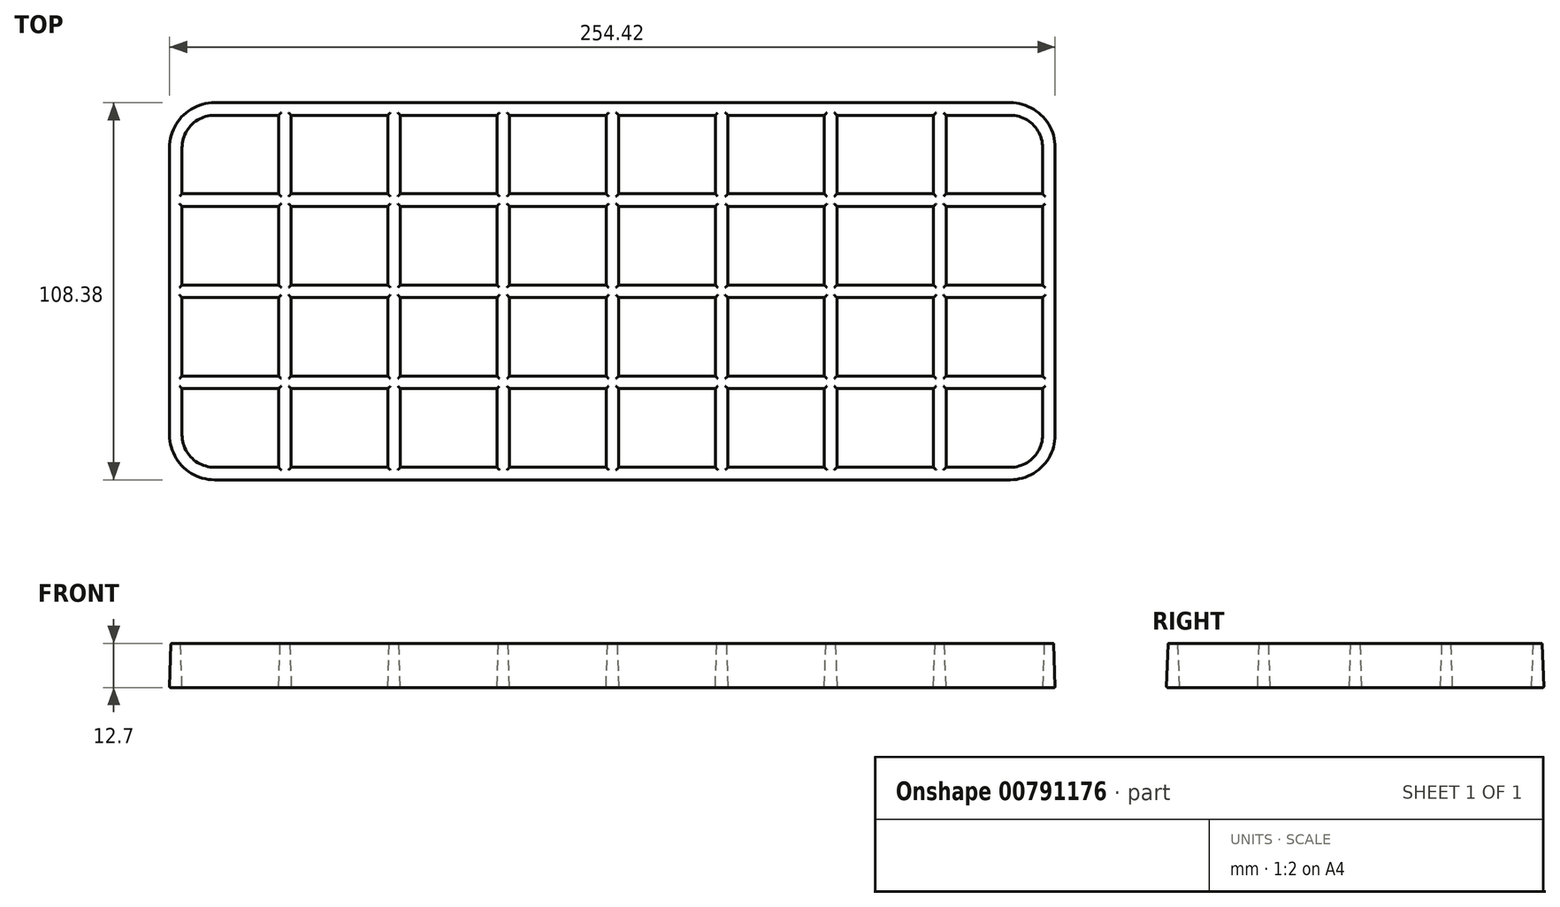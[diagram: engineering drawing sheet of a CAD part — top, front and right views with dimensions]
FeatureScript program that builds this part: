
annotation { "Feature Type Name" : "Feature", "Feature Type Description" : "" }
export const myFeature = defineFeature(function(context is Context, id is Id, definition is map)
    precondition{}
    {
        {
            var Q0;
            Q0=qCreatedBy(makeId("Top.planeOp"),FACE);
            var sketch = newSketch(context, id + "F0", { "sketchPlane" : qUnion([Q0])});
            skLineSegment(sketch, "E0.bottom", {"start": v(114.3, 53.98) * mm, "end": v(-114.3, 53.98) * mm});
            skLineSegment(sketch, "E0.top", {"start": v(114.3, -53.98) * mm, "end": v(-114.3, -53.98) * mm});
            skLineSegment(sketch, "E0.left", {"start": v(127, 41.27) * mm, "end": v(127, -41.27) * mm});
            skLineSegment(sketch, "E0.right", {"start": v(-127, 41.27) * mm, "end": v(-127, -41.27) * mm});
            skPoint(sketch, "E0.middle", {"position": v(0, 0) * mm});
            skLineSegment(sketch, "E1", {"start": v(-123.83, 26.2) * mm, "end": v(123.82, 26.2) * mm, "construction": true});
            skLineSegment(sketch, "E2", {"start": v(-123.82, 0) * mm, "end": v(123.82, 0) * mm, "construction": true});
            skLineSegment(sketch, "E3", {"start": v(-123.82, -26.2) * mm, "end": v(123.82, -26.2) * mm, "construction": true});
            skLineSegment(sketch, "E4", {"start": v(-94.06, 50.8) * mm, "end": v(-94.06, -50.8) * mm, "construction": true});
            skLineSegment(sketch, "E5", {"start": v(-62.7, 50.8) * mm, "end": v(-62.7, -50.8) * mm, "construction": true});
            skLineSegment(sketch, "E6", {"start": v(-31.35, 50.8) * mm, "end": v(-31.35, -50.8) * mm, "construction": true});
            skLineSegment(sketch, "E7", {"start": v(0, 50.8) * mm, "end": v(0, -50.8) * mm, "construction": true});
            skLineSegment(sketch, "E8", {"start": v(31.35, 50.8) * mm, "end": v(31.35, -50.8) * mm, "construction": true});
            skLineSegment(sketch, "E9", {"start": v(62.7, -50.8) * mm, "end": v(62.7, 50.8) * mm, "construction": true});
            skLineSegment(sketch, "E10", {"start": v(94.06, 50.8) * mm, "end": v(94.06, -50.8) * mm, "construction": true});
            skLineSegment(sketch, "E11.bottom", {"start": v(123.82, 27.78) * mm, "end": v(-123.83, 27.78) * mm});
            skLineSegment(sketch, "E11.top", {"start": v(123.82, 24.6) * mm, "end": v(-123.83, 24.6) * mm});
            skLineSegment(sketch, "E11.left", {"start": v(123.82, 27.78) * mm, "end": v(123.82, 24.6) * mm});
            skLineSegment(sketch, "E11.right", {"start": v(-123.82, 27.78) * mm, "end": v(-123.82, 24.6) * mm});
            skPoint(sketch, "E11.middle", {"position": v(0, 26.2) * mm});
            skLineSegment(sketch, "E12.bottom", {"start": v(123.82, 1.59) * mm, "end": v(-123.82, 1.59) * mm});
            skLineSegment(sketch, "E12.top", {"start": v(123.82, -1.59) * mm, "end": v(-123.82, -1.59) * mm});
            skLineSegment(sketch, "E12.left", {"start": v(123.82, 1.59) * mm, "end": v(123.82, -1.59) * mm});
            skLineSegment(sketch, "E12.right", {"start": v(-123.82, 1.59) * mm, "end": v(-123.82, -1.59) * mm});
            skLineSegment(sketch, "E13.bottom", {"start": v(123.82, -24.6) * mm, "end": v(-123.82, -24.6) * mm});
            skLineSegment(sketch, "E13.top", {"start": v(123.82, -27.78) * mm, "end": v(-123.82, -27.78) * mm});
            skLineSegment(sketch, "E13.left", {"start": v(123.82, -24.6) * mm, "end": v(123.82, -27.78) * mm});
            skLineSegment(sketch, "E13.right", {"start": v(-123.82, -24.6) * mm, "end": v(-123.82, -27.78) * mm});
            skPoint(sketch, "E13.middle", {"position": v(0, -26.2) * mm});
            skLineSegment(sketch, "E14.bottom", {"start": v(-92.47, 50.8) * mm, "end": v(-95.65, 50.8) * mm});
            skLineSegment(sketch, "E14.top", {"start": v(-92.47, -50.8) * mm, "end": v(-95.65, -50.8) * mm});
            skLineSegment(sketch, "E14.left", {"start": v(-92.47, 50.8) * mm, "end": v(-92.47, -50.8) * mm});
            skLineSegment(sketch, "E14.right", {"start": v(-95.65, 50.8) * mm, "end": v(-95.65, -50.8) * mm});
            skPoint(sketch, "E14.middle", {"position": v(-94.06, 0) * mm});
            skLineSegment(sketch, "E15.bottom", {"start": v(-61.12, 50.8) * mm, "end": v(-64.3, 50.8) * mm});
            skLineSegment(sketch, "E15.top", {"start": v(-61.12, -50.8) * mm, "end": v(-64.3, -50.8) * mm});
            skLineSegment(sketch, "E15.left", {"start": v(-61.12, 50.8) * mm, "end": v(-61.12, -50.8) * mm});
            skLineSegment(sketch, "E15.right", {"start": v(-64.3, 50.8) * mm, "end": v(-64.3, -50.8) * mm});
            skPoint(sketch, "E15.middle", {"position": v(-62.7, 0) * mm});
            skLineSegment(sketch, "E16.bottom", {"start": v(-29.77, 50.8) * mm, "end": v(-32.94, 50.8) * mm});
            skLineSegment(sketch, "E16.top", {"start": v(-29.77, -50.8) * mm, "end": v(-32.94, -50.8) * mm});
            skLineSegment(sketch, "E16.left", {"start": v(-29.77, 50.8) * mm, "end": v(-29.77, -50.8) * mm});
            skLineSegment(sketch, "E16.right", {"start": v(-32.94, 50.8) * mm, "end": v(-32.94, -50.8) * mm});
            skPoint(sketch, "E16.middle", {"position": v(-31.35, 0) * mm});
            skLineSegment(sketch, "E17.bottom", {"start": v(1.59, 50.8) * mm, "end": v(-1.59, 50.8) * mm});
            skLineSegment(sketch, "E17.top", {"start": v(1.59, -50.8) * mm, "end": v(-1.59, -50.8) * mm});
            skLineSegment(sketch, "E17.left", {"start": v(1.59, 50.8) * mm, "end": v(1.59, -50.8) * mm});
            skLineSegment(sketch, "E17.right", {"start": v(-1.59, 50.8) * mm, "end": v(-1.59, -50.8) * mm});
            skLineSegment(sketch, "E18.bottom", {"start": v(32.94, 50.8) * mm, "end": v(29.77, 50.8) * mm});
            skLineSegment(sketch, "E18.top", {"start": v(32.94, -50.8) * mm, "end": v(29.77, -50.8) * mm});
            skLineSegment(sketch, "E18.left", {"start": v(32.94, 50.8) * mm, "end": v(32.94, -50.8) * mm});
            skLineSegment(sketch, "E18.right", {"start": v(29.77, 50.8) * mm, "end": v(29.77, -50.8) * mm});
            skPoint(sketch, "E18.middle", {"position": v(31.35, 0) * mm});
            skLineSegment(sketch, "E19.bottom", {"start": v(64.3, 50.8) * mm, "end": v(61.12, 50.8) * mm});
            skLineSegment(sketch, "E19.top", {"start": v(64.3, -50.8) * mm, "end": v(61.12, -50.8) * mm});
            skLineSegment(sketch, "E19.left", {"start": v(64.3, 50.8) * mm, "end": v(64.3, -50.8) * mm});
            skLineSegment(sketch, "E19.right", {"start": v(61.12, 50.8) * mm, "end": v(61.12, -50.8) * mm});
            skPoint(sketch, "E19.middle", {"position": v(62.7, 0) * mm});
            skLineSegment(sketch, "E20.bottom", {"start": v(95.65, 50.8) * mm, "end": v(92.47, 50.8) * mm});
            skLineSegment(sketch, "E20.top", {"start": v(95.65, -50.8) * mm, "end": v(92.47, -50.8) * mm});
            skLineSegment(sketch, "E20.left", {"start": v(95.65, 50.8) * mm, "end": v(95.65, -50.8) * mm});
            skLineSegment(sketch, "E20.right", {"start": v(92.47, 50.8) * mm, "end": v(92.47, -50.8) * mm});
            skPoint(sketch, "E20.middle", {"position": v(94.06, 0) * mm});
            skPoint(sketch, "E21.visualSharp", {"position": v(127, 53.98) * mm});
            skArc(sketch, "E21.filletArc", {"start": v(127, 41.27) * mm, "mid": v(123.28, 50.26) * mm, "end": v(114.3, 53.98) * mm});
            skArc(sketch, "E22.0", {"start": v(123.83, 41.27) * mm, "mid": v(121.04, 48.01) * mm, "end": v(114.3, 50.8) * mm});
            skLineSegment(sketch, "E23.trimOffspring", {"start": v(123.82, 41.27) * mm, "end": v(123.82, -41.28) * mm});
            skLineSegment(sketch, "E24.trimOffspring", {"start": v(114.3, 50.8) * mm, "end": v(-114.3, 50.8) * mm});
            skPoint(sketch, "E25.visualSharp", {"position": v(127, -53.98) * mm});
            skArc(sketch, "E25.filletArc", {"start": v(114.3, -53.98) * mm, "mid": v(123.28, -50.26) * mm, "end": v(127, -41.27) * mm});
            skArc(sketch, "E26.0", {"start": v(114.3, -50.8) * mm, "mid": v(121.04, -48.01) * mm, "end": v(123.83, -41.28) * mm});
            skLineSegment(sketch, "E27.trimOffspring", {"start": v(114.3, -50.8) * mm, "end": v(-114.3, -50.8) * mm});
            skPoint(sketch, "E28.visualSharp", {"position": v(-127, -53.98) * mm});
            skArc(sketch, "E28.filletArc", {"start": v(-127, -41.27) * mm, "mid": v(-123.28, -50.26) * mm, "end": v(-114.3, -53.98) * mm});
            skArc(sketch, "E29.0", {"start": v(-123.83, -41.27) * mm, "mid": v(-121.04, -48.01) * mm, "end": v(-114.3, -50.8) * mm});
            skPoint(sketch, "E30.visualSharp", {"position": v(-127, 53.97) * mm});
            skArc(sketch, "E30.filletArc", {"start": v(-114.3, 53.98) * mm, "mid": v(-123.28, 50.26) * mm, "end": v(-127, 41.27) * mm});
            skArc(sketch, "E31.0", {"start": v(-114.3, 50.8) * mm, "mid": v(-121.04, 48.01) * mm, "end": v(-123.83, 41.27) * mm});
            skLineSegment(sketch, "E32.trimOffspring", {"start": v(-123.82, 41.27) * mm, "end": v(-123.82, -41.27) * mm});
            skSolve(sketch);
        }
        {
            var Q0;
            Q0=qSketchRegion(id+"F0",true);
            var Q1;
            {var subQ5=sQuery(id+"F0.wireOp",EDGE,"E14.bottom");Q1=makeQuery(id+"F0.imprint","IMPRINT",FACE,{"disambiguationData":[TD([[makeQuery(id+"F0.imprint","IMPRINT",EDGE,{"derivedFrom":subQ5}),1.0]])]});}
            var Q2;
            {var subQ5=sQuery(id+"F0.wireOp",EDGE,"E15.bottom");Q2=makeQuery(id+"F0.imprint","IMPRINT",FACE,{"disambiguationData":[TD([[makeQuery(id+"F0.imprint","IMPRINT",EDGE,{"derivedFrom":subQ5}),1.0]])]});}
            var Q3;
            {var subQ5=sQuery(id+"F0.wireOp",EDGE,"E16.bottom");Q3=makeQuery(id+"F0.imprint","IMPRINT",FACE,{"disambiguationData":[TD([[makeQuery(id+"F0.imprint","IMPRINT",EDGE,{"derivedFrom":subQ5}),1.0]])]});}
            var Q4;
            {var subQ5=sQuery(id+"F0.wireOp",EDGE,"E17.bottom");Q4=makeQuery(id+"F0.imprint","IMPRINT",FACE,{"disambiguationData":[TD([[makeQuery(id+"F0.imprint","IMPRINT",EDGE,{"derivedFrom":subQ5}),1.0]])]});}
            var Q5;
            {var subQ5=sQuery(id+"F0.wireOp",EDGE,"E18.bottom");Q5=makeQuery(id+"F0.imprint","IMPRINT",FACE,{"disambiguationData":[TD([[makeQuery(id+"F0.imprint","IMPRINT",EDGE,{"derivedFrom":subQ5}),1.0]])]});}
            var Q6;
            {var subQ5=sQuery(id+"F0.wireOp",EDGE,"E19.bottom");Q6=makeQuery(id+"F0.imprint","IMPRINT",FACE,{"disambiguationData":[TD([[makeQuery(id+"F0.imprint","IMPRINT",EDGE,{"derivedFrom":subQ5}),1.0]])]});}
            var Q7;
            {var subQ5=sQuery(id+"F0.wireOp",EDGE,"E20.bottom");Q7=makeQuery(id+"F0.imprint","IMPRINT",FACE,{"disambiguationData":[TD([[makeQuery(id+"F0.imprint","IMPRINT",EDGE,{"derivedFrom":subQ5}),1.0]])]});}
            var Q8;
            {var subQ0=sQuery(id+"F0.wireOp",EDGE,"E11.left");Q8=makeQuery(id+"F0.imprint","IMPRINT",FACE,{"disambiguationData":[TD([[makeQuery(id+"F0.imprint","IMPRINT",EDGE,{"derivedFrom":subQ0}),-1.0]])]});}
            var Q9;
            {var subQ0=sQuery(id+"F0.wireOp",EDGE,"E20.left");var subQ1=sQuery(id+"F0.wireOp",EDGE,"E11.bottom");var subQ2=makeQuery(id+"F0.imprint","INTERSECT",VERTEX,{"derivedFrom":[subQ1,subQ0]});Q9=makeQuery(id+"F0.imprint","IMPRINT",FACE,{"disambiguationData":[TD([[makeQuery(id+"F0.imprint","IMPRINT",EDGE,{"disambiguationData":[TD([[subQ2,-1.0]])],"derivedFrom":subQ1}),1.0]])]});}
            var Q10;
            {var subQ0=sQuery(id+"F0.wireOp",EDGE,"E20.right");var subQ1=sQuery(id+"F0.wireOp",EDGE,"E11.bottom");var subQ2=makeQuery(id+"F0.imprint","INTERSECT",VERTEX,{"derivedFrom":[subQ1,subQ0]});Q10=makeQuery(id+"F0.imprint","IMPRINT",FACE,{"disambiguationData":[TD([[makeQuery(id+"F0.imprint","IMPRINT",EDGE,{"disambiguationData":[TD([[subQ2,-1.0]])],"derivedFrom":subQ1}),1.0]])]});}
            var Q11;
            {var subQ0=sQuery(id+"F0.wireOp",EDGE,"E19.left");var subQ1=sQuery(id+"F0.wireOp",EDGE,"E11.bottom");var subQ2=makeQuery(id+"F0.imprint","INTERSECT",VERTEX,{"derivedFrom":[subQ1,subQ0]});Q11=makeQuery(id+"F0.imprint","IMPRINT",FACE,{"disambiguationData":[TD([[makeQuery(id+"F0.imprint","IMPRINT",EDGE,{"disambiguationData":[TD([[subQ2,-1.0]])],"derivedFrom":subQ1}),1.0]])]});}
            var Q12;
            {var subQ0=sQuery(id+"F0.wireOp",EDGE,"E18.left");var subQ1=sQuery(id+"F0.wireOp",EDGE,"E11.bottom");var subQ2=makeQuery(id+"F0.imprint","INTERSECT",VERTEX,{"derivedFrom":[subQ1,subQ0]});Q12=makeQuery(id+"F0.imprint","IMPRINT",FACE,{"disambiguationData":[TD([[makeQuery(id+"F0.imprint","IMPRINT",EDGE,{"disambiguationData":[TD([[subQ2,-1.0]])],"derivedFrom":subQ1}),1.0]])]});}
            var Q13;
            {var subQ0=sQuery(id+"F0.wireOp",EDGE,"E19.right");var subQ1=sQuery(id+"F0.wireOp",EDGE,"E11.bottom");var subQ2=makeQuery(id+"F0.imprint","INTERSECT",VERTEX,{"derivedFrom":[subQ1,subQ0]});Q13=makeQuery(id+"F0.imprint","IMPRINT",FACE,{"disambiguationData":[TD([[makeQuery(id+"F0.imprint","IMPRINT",EDGE,{"disambiguationData":[TD([[subQ2,-1.0]])],"derivedFrom":subQ1}),1.0]])]});}
            var Q14;
            {var subQ0=sQuery(id+"F0.wireOp",EDGE,"E18.right");var subQ1=sQuery(id+"F0.wireOp",EDGE,"E11.bottom");var subQ2=makeQuery(id+"F0.imprint","INTERSECT",VERTEX,{"derivedFrom":[subQ1,subQ0]});Q14=makeQuery(id+"F0.imprint","IMPRINT",FACE,{"disambiguationData":[TD([[makeQuery(id+"F0.imprint","IMPRINT",EDGE,{"disambiguationData":[TD([[subQ2,-1.0]])],"derivedFrom":subQ1}),1.0]])]});}
            var Q15;
            {var subQ0=sQuery(id+"F0.wireOp",EDGE,"E17.left");var subQ1=sQuery(id+"F0.wireOp",EDGE,"E11.bottom");var subQ2=makeQuery(id+"F0.imprint","INTERSECT",VERTEX,{"derivedFrom":[subQ1,subQ0]});Q15=makeQuery(id+"F0.imprint","IMPRINT",FACE,{"disambiguationData":[TD([[makeQuery(id+"F0.imprint","IMPRINT",EDGE,{"disambiguationData":[TD([[subQ2,-1.0]])],"derivedFrom":subQ1}),1.0]])]});}
            var Q16;
            {var subQ0=sQuery(id+"F0.wireOp",EDGE,"E17.right");var subQ1=sQuery(id+"F0.wireOp",EDGE,"E11.bottom");var subQ2=makeQuery(id+"F0.imprint","INTERSECT",VERTEX,{"derivedFrom":[subQ1,subQ0]});Q16=makeQuery(id+"F0.imprint","IMPRINT",FACE,{"disambiguationData":[TD([[makeQuery(id+"F0.imprint","IMPRINT",EDGE,{"disambiguationData":[TD([[subQ2,-1.0]])],"derivedFrom":subQ1}),1.0]])]});}
            var Q17;
            {var subQ0=sQuery(id+"F0.wireOp",EDGE,"E16.left");var subQ1=sQuery(id+"F0.wireOp",EDGE,"E11.bottom");var subQ2=makeQuery(id+"F0.imprint","INTERSECT",VERTEX,{"derivedFrom":[subQ1,subQ0]});Q17=makeQuery(id+"F0.imprint","IMPRINT",FACE,{"disambiguationData":[TD([[makeQuery(id+"F0.imprint","IMPRINT",EDGE,{"disambiguationData":[TD([[subQ2,-1.0]])],"derivedFrom":subQ1}),1.0]])]});}
            var Q18;
            {var subQ0=sQuery(id+"F0.wireOp",EDGE,"E16.right");var subQ1=sQuery(id+"F0.wireOp",EDGE,"E11.bottom");var subQ2=makeQuery(id+"F0.imprint","INTERSECT",VERTEX,{"derivedFrom":[subQ1,subQ0]});Q18=makeQuery(id+"F0.imprint","IMPRINT",FACE,{"disambiguationData":[TD([[makeQuery(id+"F0.imprint","IMPRINT",EDGE,{"disambiguationData":[TD([[subQ2,-1.0]])],"derivedFrom":subQ1}),1.0]])]});}
            var Q19;
            {var subQ0=sQuery(id+"F0.wireOp",EDGE,"E15.left");var subQ1=sQuery(id+"F0.wireOp",EDGE,"E11.bottom");var subQ2=makeQuery(id+"F0.imprint","INTERSECT",VERTEX,{"derivedFrom":[subQ1,subQ0]});Q19=makeQuery(id+"F0.imprint","IMPRINT",FACE,{"disambiguationData":[TD([[makeQuery(id+"F0.imprint","IMPRINT",EDGE,{"disambiguationData":[TD([[subQ2,-1.0]])],"derivedFrom":subQ1}),1.0]])]});}
            var Q20;
            {var subQ0=sQuery(id+"F0.wireOp",EDGE,"E15.right");var subQ1=sQuery(id+"F0.wireOp",EDGE,"E11.bottom");var subQ2=makeQuery(id+"F0.imprint","INTERSECT",VERTEX,{"derivedFrom":[subQ1,subQ0]});Q20=makeQuery(id+"F0.imprint","IMPRINT",FACE,{"disambiguationData":[TD([[makeQuery(id+"F0.imprint","IMPRINT",EDGE,{"disambiguationData":[TD([[subQ2,-1.0]])],"derivedFrom":subQ1}),1.0]])]});}
            var Q21;
            {var subQ0=sQuery(id+"F0.wireOp",EDGE,"E14.left");var subQ1=sQuery(id+"F0.wireOp",EDGE,"E11.bottom");var subQ2=makeQuery(id+"F0.imprint","INTERSECT",VERTEX,{"derivedFrom":[subQ1,subQ0]});Q21=makeQuery(id+"F0.imprint","IMPRINT",FACE,{"disambiguationData":[TD([[makeQuery(id+"F0.imprint","IMPRINT",EDGE,{"disambiguationData":[TD([[subQ2,-1.0]])],"derivedFrom":subQ1}),1.0]])]});}
            var Q22;
            {var subQ0=sQuery(id+"F0.wireOp",EDGE,"E11.right");Q22=makeQuery(id+"F0.imprint","IMPRINT",FACE,{"disambiguationData":[TD([[makeQuery(id+"F0.imprint","IMPRINT",EDGE,{"derivedFrom":subQ0}),1.0]])]});}
            var Q23;
            {var subQ0=sQuery(id+"F0.wireOp",EDGE,"E14.left");var subQ1=sQuery(id+"F0.wireOp",EDGE,"E11.top");var subQ2=makeQuery(id+"F0.imprint","INTERSECT",VERTEX,{"derivedFrom":[subQ1,subQ0]});Q23=makeQuery(id+"F0.imprint","IMPRINT",FACE,{"disambiguationData":[TD([[makeQuery(id+"F0.imprint","IMPRINT",EDGE,{"disambiguationData":[TD([[subQ2,-1.0]])],"derivedFrom":subQ1}),1.0]])]});}
            var Q24;
            {var subQ0=sQuery(id+"F0.wireOp",EDGE,"E15.left");var subQ1=sQuery(id+"F0.wireOp",EDGE,"E11.top");var subQ2=makeQuery(id+"F0.imprint","INTERSECT",VERTEX,{"derivedFrom":[subQ1,subQ0]});Q24=makeQuery(id+"F0.imprint","IMPRINT",FACE,{"disambiguationData":[TD([[makeQuery(id+"F0.imprint","IMPRINT",EDGE,{"disambiguationData":[TD([[subQ2,-1.0]])],"derivedFrom":subQ1}),1.0]])]});}
            var Q25;
            {var subQ0=sQuery(id+"F0.wireOp",EDGE,"E16.left");var subQ1=sQuery(id+"F0.wireOp",EDGE,"E11.top");var subQ2=makeQuery(id+"F0.imprint","INTERSECT",VERTEX,{"derivedFrom":[subQ1,subQ0]});Q25=makeQuery(id+"F0.imprint","IMPRINT",FACE,{"disambiguationData":[TD([[makeQuery(id+"F0.imprint","IMPRINT",EDGE,{"disambiguationData":[TD([[subQ2,-1.0]])],"derivedFrom":subQ1}),1.0]])]});}
            var Q26;
            {var subQ0=sQuery(id+"F0.wireOp",EDGE,"E18.left");var subQ1=sQuery(id+"F0.wireOp",EDGE,"E11.top");var subQ2=makeQuery(id+"F0.imprint","INTERSECT",VERTEX,{"derivedFrom":[subQ1,subQ0]});Q26=makeQuery(id+"F0.imprint","IMPRINT",FACE,{"disambiguationData":[TD([[makeQuery(id+"F0.imprint","IMPRINT",EDGE,{"disambiguationData":[TD([[subQ2,-1.0]])],"derivedFrom":subQ1}),1.0]])]});}
            var Q27;
            {var subQ0=sQuery(id+"F0.wireOp",EDGE,"E19.left");var subQ1=sQuery(id+"F0.wireOp",EDGE,"E11.top");var subQ2=makeQuery(id+"F0.imprint","INTERSECT",VERTEX,{"derivedFrom":[subQ1,subQ0]});Q27=makeQuery(id+"F0.imprint","IMPRINT",FACE,{"disambiguationData":[TD([[makeQuery(id+"F0.imprint","IMPRINT",EDGE,{"disambiguationData":[TD([[subQ2,-1.0]])],"derivedFrom":subQ1}),1.0]])]});}
            var Q28;
            {var subQ0=sQuery(id+"F0.wireOp",EDGE,"E20.left");var subQ1=sQuery(id+"F0.wireOp",EDGE,"E11.top");var subQ2=makeQuery(id+"F0.imprint","INTERSECT",VERTEX,{"derivedFrom":[subQ1,subQ0]});Q28=makeQuery(id+"F0.imprint","IMPRINT",FACE,{"disambiguationData":[TD([[makeQuery(id+"F0.imprint","IMPRINT",EDGE,{"disambiguationData":[TD([[subQ2,-1.0]])],"derivedFrom":subQ1}),1.0]])]});}
            var Q29;
            {var subQ0=sQuery(id+"F0.wireOp",EDGE,"E20.left");var subQ1=sQuery(id+"F0.wireOp",EDGE,"E12.bottom");var subQ2=makeQuery(id+"F0.imprint","INTERSECT",VERTEX,{"derivedFrom":[subQ1,subQ0]});Q29=makeQuery(id+"F0.imprint","IMPRINT",FACE,{"disambiguationData":[TD([[makeQuery(id+"F0.imprint","IMPRINT",EDGE,{"disambiguationData":[TD([[subQ2,-1.0]])],"derivedFrom":subQ1}),1.0]])]});}
            var Q30;
            {var subQ0=sQuery(id+"F0.wireOp",EDGE,"E12.left");Q30=makeQuery(id+"F0.imprint","IMPRINT",FACE,{"disambiguationData":[TD([[makeQuery(id+"F0.imprint","IMPRINT",EDGE,{"derivedFrom":subQ0}),-1.0]])]});}
            var Q31;
            {var subQ0=sQuery(id+"F0.wireOp",EDGE,"E20.left");var subQ1=sQuery(id+"F0.wireOp",EDGE,"E12.top");var subQ2=makeQuery(id+"F0.imprint","INTERSECT",VERTEX,{"derivedFrom":[subQ1,subQ0]});Q31=makeQuery(id+"F0.imprint","IMPRINT",FACE,{"disambiguationData":[TD([[makeQuery(id+"F0.imprint","IMPRINT",EDGE,{"disambiguationData":[TD([[subQ2,-1.0]])],"derivedFrom":subQ1}),1.0]])]});}
            var Q32;
            {var subQ0=sQuery(id+"F0.wireOp",EDGE,"E20.right");var subQ1=sQuery(id+"F0.wireOp",EDGE,"E12.bottom");var subQ2=makeQuery(id+"F0.imprint","INTERSECT",VERTEX,{"derivedFrom":[subQ1,subQ0]});Q32=makeQuery(id+"F0.imprint","IMPRINT",FACE,{"disambiguationData":[TD([[makeQuery(id+"F0.imprint","IMPRINT",EDGE,{"disambiguationData":[TD([[subQ2,-1.0]])],"derivedFrom":subQ1}),1.0]])]});}
            var Q33;
            {var subQ0=sQuery(id+"F0.wireOp",EDGE,"E19.left");var subQ1=sQuery(id+"F0.wireOp",EDGE,"E12.top");var subQ2=makeQuery(id+"F0.imprint","INTERSECT",VERTEX,{"derivedFrom":[subQ1,subQ0]});Q33=makeQuery(id+"F0.imprint","IMPRINT",FACE,{"disambiguationData":[TD([[makeQuery(id+"F0.imprint","IMPRINT",EDGE,{"disambiguationData":[TD([[subQ2,-1.0]])],"derivedFrom":subQ1}),1.0]])]});}
            var Q34;
            {var subQ0=sQuery(id+"F0.wireOp",EDGE,"E19.left");var subQ1=sQuery(id+"F0.wireOp",EDGE,"E12.bottom");var subQ2=makeQuery(id+"F0.imprint","INTERSECT",VERTEX,{"derivedFrom":[subQ1,subQ0]});Q34=makeQuery(id+"F0.imprint","IMPRINT",FACE,{"disambiguationData":[TD([[makeQuery(id+"F0.imprint","IMPRINT",EDGE,{"disambiguationData":[TD([[subQ2,-1.0]])],"derivedFrom":subQ1}),1.0]])]});}
            var Q35;
            {var subQ0=sQuery(id+"F0.wireOp",EDGE,"E19.right");var subQ1=sQuery(id+"F0.wireOp",EDGE,"E12.bottom");var subQ2=makeQuery(id+"F0.imprint","INTERSECT",VERTEX,{"derivedFrom":[subQ1,subQ0]});Q35=makeQuery(id+"F0.imprint","IMPRINT",FACE,{"disambiguationData":[TD([[makeQuery(id+"F0.imprint","IMPRINT",EDGE,{"disambiguationData":[TD([[subQ2,-1.0]])],"derivedFrom":subQ1}),1.0]])]});}
            var Q36;
            {var subQ0=sQuery(id+"F0.wireOp",EDGE,"E18.left");var subQ1=sQuery(id+"F0.wireOp",EDGE,"E12.bottom");var subQ2=makeQuery(id+"F0.imprint","INTERSECT",VERTEX,{"derivedFrom":[subQ1,subQ0]});Q36=makeQuery(id+"F0.imprint","IMPRINT",FACE,{"disambiguationData":[TD([[makeQuery(id+"F0.imprint","IMPRINT",EDGE,{"disambiguationData":[TD([[subQ2,-1.0]])],"derivedFrom":subQ1}),1.0]])]});}
            var Q37;
            {var subQ0=sQuery(id+"F0.wireOp",EDGE,"E16.right");var subQ1=sQuery(id+"F0.wireOp",EDGE,"E12.bottom");var subQ2=makeQuery(id+"F0.imprint","INTERSECT",VERTEX,{"derivedFrom":[subQ1,subQ0]});Q37=makeQuery(id+"F0.imprint","IMPRINT",FACE,{"disambiguationData":[TD([[makeQuery(id+"F0.imprint","IMPRINT",EDGE,{"disambiguationData":[TD([[subQ2,-1.0]])],"derivedFrom":subQ1}),1.0]])]});}
            var Q38;
            {var subQ0=sQuery(id+"F0.wireOp",EDGE,"E15.left");var subQ1=sQuery(id+"F0.wireOp",EDGE,"E12.bottom");var subQ2=makeQuery(id+"F0.imprint","INTERSECT",VERTEX,{"derivedFrom":[subQ1,subQ0]});Q38=makeQuery(id+"F0.imprint","IMPRINT",FACE,{"disambiguationData":[TD([[makeQuery(id+"F0.imprint","IMPRINT",EDGE,{"disambiguationData":[TD([[subQ2,-1.0]])],"derivedFrom":subQ1}),1.0]])]});}
            var Q39;
            {var subQ0=sQuery(id+"F0.wireOp",EDGE,"E15.right");var subQ1=sQuery(id+"F0.wireOp",EDGE,"E12.bottom");var subQ2=makeQuery(id+"F0.imprint","INTERSECT",VERTEX,{"derivedFrom":[subQ1,subQ0]});Q39=makeQuery(id+"F0.imprint","IMPRINT",FACE,{"disambiguationData":[TD([[makeQuery(id+"F0.imprint","IMPRINT",EDGE,{"disambiguationData":[TD([[subQ2,-1.0]])],"derivedFrom":subQ1}),1.0]])]});}
            var Q40;
            {var subQ0=sQuery(id+"F0.wireOp",EDGE,"E12.right");Q40=makeQuery(id+"F0.imprint","IMPRINT",FACE,{"disambiguationData":[TD([[makeQuery(id+"F0.imprint","IMPRINT",EDGE,{"derivedFrom":subQ0}),1.0]])]});}
            var Q41;
            {var subQ0=sQuery(id+"F0.wireOp",EDGE,"E14.left");var subQ1=sQuery(id+"F0.wireOp",EDGE,"E12.bottom");var subQ2=makeQuery(id+"F0.imprint","INTERSECT",VERTEX,{"derivedFrom":[subQ1,subQ0]});Q41=makeQuery(id+"F0.imprint","IMPRINT",FACE,{"disambiguationData":[TD([[makeQuery(id+"F0.imprint","IMPRINT",EDGE,{"disambiguationData":[TD([[subQ2,-1.0]])],"derivedFrom":subQ1}),1.0]])]});}
            var Q42;
            {var subQ0=sQuery(id+"F0.wireOp",EDGE,"E16.left");var subQ1=sQuery(id+"F0.wireOp",EDGE,"E12.bottom");var subQ2=makeQuery(id+"F0.imprint","INTERSECT",VERTEX,{"derivedFrom":[subQ1,subQ0]});Q42=makeQuery(id+"F0.imprint","IMPRINT",FACE,{"disambiguationData":[TD([[makeQuery(id+"F0.imprint","IMPRINT",EDGE,{"disambiguationData":[TD([[subQ2,-1.0]])],"derivedFrom":subQ1}),1.0]])]});}
            var Q43;
            {var subQ0=sQuery(id+"F0.wireOp",EDGE,"E14.left");var subQ1=sQuery(id+"F0.wireOp",EDGE,"E12.top");var subQ2=makeQuery(id+"F0.imprint","INTERSECT",VERTEX,{"derivedFrom":[subQ1,subQ0]});Q43=makeQuery(id+"F0.imprint","IMPRINT",FACE,{"disambiguationData":[TD([[makeQuery(id+"F0.imprint","IMPRINT",EDGE,{"disambiguationData":[TD([[subQ2,-1.0]])],"derivedFrom":subQ1}),1.0]])]});}
            var Q44;
            {var subQ0=sQuery(id+"F0.wireOp",EDGE,"E15.left");var subQ1=sQuery(id+"F0.wireOp",EDGE,"E12.top");var subQ2=makeQuery(id+"F0.imprint","INTERSECT",VERTEX,{"derivedFrom":[subQ1,subQ0]});Q44=makeQuery(id+"F0.imprint","IMPRINT",FACE,{"disambiguationData":[TD([[makeQuery(id+"F0.imprint","IMPRINT",EDGE,{"disambiguationData":[TD([[subQ2,-1.0]])],"derivedFrom":subQ1}),1.0]])]});}
            var Q45;
            {var subQ0=sQuery(id+"F0.wireOp",EDGE,"E16.left");var subQ1=sQuery(id+"F0.wireOp",EDGE,"E12.top");var subQ2=makeQuery(id+"F0.imprint","INTERSECT",VERTEX,{"derivedFrom":[subQ1,subQ0]});Q45=makeQuery(id+"F0.imprint","IMPRINT",FACE,{"disambiguationData":[TD([[makeQuery(id+"F0.imprint","IMPRINT",EDGE,{"disambiguationData":[TD([[subQ2,-1.0]])],"derivedFrom":subQ1}),1.0]])]});}
            var Q46;
            {var subQ0=sQuery(id+"F0.wireOp",EDGE,"E18.left");var subQ1=sQuery(id+"F0.wireOp",EDGE,"E12.top");var subQ2=makeQuery(id+"F0.imprint","INTERSECT",VERTEX,{"derivedFrom":[subQ1,subQ0]});Q46=makeQuery(id+"F0.imprint","IMPRINT",FACE,{"disambiguationData":[TD([[makeQuery(id+"F0.imprint","IMPRINT",EDGE,{"disambiguationData":[TD([[subQ2,-1.0]])],"derivedFrom":subQ1}),1.0]])]});}
            var Q47;
            {var subQ0=sQuery(id+"F0.wireOp",EDGE,"E13.left");Q47=makeQuery(id+"F0.imprint","IMPRINT",FACE,{"disambiguationData":[TD([[makeQuery(id+"F0.imprint","IMPRINT",EDGE,{"derivedFrom":subQ0}),-1.0]])]});}
            var Q48;
            {var subQ0=sQuery(id+"F0.wireOp",EDGE,"E20.left");var subQ1=sQuery(id+"F0.wireOp",EDGE,"E13.bottom");var subQ2=makeQuery(id+"F0.imprint","INTERSECT",VERTEX,{"derivedFrom":[subQ1,subQ0]});Q48=makeQuery(id+"F0.imprint","IMPRINT",FACE,{"disambiguationData":[TD([[makeQuery(id+"F0.imprint","IMPRINT",EDGE,{"disambiguationData":[TD([[subQ2,-1.0]])],"derivedFrom":subQ1}),1.0]])]});}
            var Q49;
            {var subQ0=sQuery(id+"F0.wireOp",EDGE,"E20.right");var subQ1=sQuery(id+"F0.wireOp",EDGE,"E13.bottom");var subQ2=makeQuery(id+"F0.imprint","INTERSECT",VERTEX,{"derivedFrom":[subQ1,subQ0]});Q49=makeQuery(id+"F0.imprint","IMPRINT",FACE,{"disambiguationData":[TD([[makeQuery(id+"F0.imprint","IMPRINT",EDGE,{"disambiguationData":[TD([[subQ2,-1.0]])],"derivedFrom":subQ1}),1.0]])]});}
            var Q50;
            {var subQ0=sQuery(id+"F0.wireOp",EDGE,"E19.left");var subQ1=sQuery(id+"F0.wireOp",EDGE,"E13.bottom");var subQ2=makeQuery(id+"F0.imprint","INTERSECT",VERTEX,{"derivedFrom":[subQ1,subQ0]});Q50=makeQuery(id+"F0.imprint","IMPRINT",FACE,{"disambiguationData":[TD([[makeQuery(id+"F0.imprint","IMPRINT",EDGE,{"disambiguationData":[TD([[subQ2,-1.0]])],"derivedFrom":subQ1}),1.0]])]});}
            var Q51;
            {var subQ0=sQuery(id+"F0.wireOp",EDGE,"E19.right");var subQ1=sQuery(id+"F0.wireOp",EDGE,"E13.bottom");var subQ2=makeQuery(id+"F0.imprint","INTERSECT",VERTEX,{"derivedFrom":[subQ1,subQ0]});Q51=makeQuery(id+"F0.imprint","IMPRINT",FACE,{"disambiguationData":[TD([[makeQuery(id+"F0.imprint","IMPRINT",EDGE,{"disambiguationData":[TD([[subQ2,-1.0]])],"derivedFrom":subQ1}),1.0]])]});}
            var Q52;
            {var subQ0=sQuery(id+"F0.wireOp",EDGE,"E18.left");var subQ1=sQuery(id+"F0.wireOp",EDGE,"E13.bottom");var subQ2=makeQuery(id+"F0.imprint","INTERSECT",VERTEX,{"derivedFrom":[subQ1,subQ0]});Q52=makeQuery(id+"F0.imprint","IMPRINT",FACE,{"disambiguationData":[TD([[makeQuery(id+"F0.imprint","IMPRINT",EDGE,{"disambiguationData":[TD([[subQ2,-1.0]])],"derivedFrom":subQ1}),1.0]])]});}
            var Q53;
            {var subQ0=sQuery(id+"F0.wireOp",EDGE,"E18.right");var subQ1=sQuery(id+"F0.wireOp",EDGE,"E13.bottom");var subQ2=makeQuery(id+"F0.imprint","INTERSECT",VERTEX,{"derivedFrom":[subQ1,subQ0]});Q53=makeQuery(id+"F0.imprint","IMPRINT",FACE,{"disambiguationData":[TD([[makeQuery(id+"F0.imprint","IMPRINT",EDGE,{"disambiguationData":[TD([[subQ2,-1.0]])],"derivedFrom":subQ1}),1.0]])]});}
            var Q54;
            {var subQ0=sQuery(id+"F0.wireOp",EDGE,"E17.left");var subQ1=sQuery(id+"F0.wireOp",EDGE,"E13.bottom");var subQ2=makeQuery(id+"F0.imprint","INTERSECT",VERTEX,{"derivedFrom":[subQ1,subQ0]});Q54=makeQuery(id+"F0.imprint","IMPRINT",FACE,{"disambiguationData":[TD([[makeQuery(id+"F0.imprint","IMPRINT",EDGE,{"disambiguationData":[TD([[subQ2,-1.0]])],"derivedFrom":subQ1}),1.0]])]});}
            var Q55;
            {var subQ0=sQuery(id+"F0.wireOp",EDGE,"E17.right");var subQ1=sQuery(id+"F0.wireOp",EDGE,"E13.bottom");var subQ2=makeQuery(id+"F0.imprint","INTERSECT",VERTEX,{"derivedFrom":[subQ1,subQ0]});Q55=makeQuery(id+"F0.imprint","IMPRINT",FACE,{"disambiguationData":[TD([[makeQuery(id+"F0.imprint","IMPRINT",EDGE,{"disambiguationData":[TD([[subQ2,-1.0]])],"derivedFrom":subQ1}),1.0]])]});}
            var Q56;
            {var subQ0=sQuery(id+"F0.wireOp",EDGE,"E16.left");var subQ1=sQuery(id+"F0.wireOp",EDGE,"E13.bottom");var subQ2=makeQuery(id+"F0.imprint","INTERSECT",VERTEX,{"derivedFrom":[subQ1,subQ0]});Q56=makeQuery(id+"F0.imprint","IMPRINT",FACE,{"disambiguationData":[TD([[makeQuery(id+"F0.imprint","IMPRINT",EDGE,{"disambiguationData":[TD([[subQ2,-1.0]])],"derivedFrom":subQ1}),1.0]])]});}
            var Q57;
            {var subQ0=sQuery(id+"F0.wireOp",EDGE,"E16.right");var subQ1=sQuery(id+"F0.wireOp",EDGE,"E13.bottom");var subQ2=makeQuery(id+"F0.imprint","INTERSECT",VERTEX,{"derivedFrom":[subQ1,subQ0]});Q57=makeQuery(id+"F0.imprint","IMPRINT",FACE,{"disambiguationData":[TD([[makeQuery(id+"F0.imprint","IMPRINT",EDGE,{"disambiguationData":[TD([[subQ2,-1.0]])],"derivedFrom":subQ1}),1.0]])]});}
            var Q58;
            {var subQ0=sQuery(id+"F0.wireOp",EDGE,"E15.left");var subQ1=sQuery(id+"F0.wireOp",EDGE,"E13.bottom");var subQ2=makeQuery(id+"F0.imprint","INTERSECT",VERTEX,{"derivedFrom":[subQ1,subQ0]});Q58=makeQuery(id+"F0.imprint","IMPRINT",FACE,{"disambiguationData":[TD([[makeQuery(id+"F0.imprint","IMPRINT",EDGE,{"disambiguationData":[TD([[subQ2,-1.0]])],"derivedFrom":subQ1}),1.0]])]});}
            var Q59;
            {var subQ0=sQuery(id+"F0.wireOp",EDGE,"E15.right");var subQ1=sQuery(id+"F0.wireOp",EDGE,"E13.bottom");var subQ2=makeQuery(id+"F0.imprint","INTERSECT",VERTEX,{"derivedFrom":[subQ1,subQ0]});Q59=makeQuery(id+"F0.imprint","IMPRINT",FACE,{"disambiguationData":[TD([[makeQuery(id+"F0.imprint","IMPRINT",EDGE,{"disambiguationData":[TD([[subQ2,-1.0]])],"derivedFrom":subQ1}),1.0]])]});}
            var Q60;
            {var subQ0=sQuery(id+"F0.wireOp",EDGE,"E14.left");var subQ1=sQuery(id+"F0.wireOp",EDGE,"E13.bottom");var subQ2=makeQuery(id+"F0.imprint","INTERSECT",VERTEX,{"derivedFrom":[subQ1,subQ0]});Q60=makeQuery(id+"F0.imprint","IMPRINT",FACE,{"disambiguationData":[TD([[makeQuery(id+"F0.imprint","IMPRINT",EDGE,{"disambiguationData":[TD([[subQ2,-1.0]])],"derivedFrom":subQ1}),1.0]])]});}
            var Q61;
            {var subQ0=sQuery(id+"F0.wireOp",EDGE,"E13.right");Q61=makeQuery(id+"F0.imprint","IMPRINT",FACE,{"disambiguationData":[TD([[makeQuery(id+"F0.imprint","IMPRINT",EDGE,{"derivedFrom":subQ0}),1.0]])]});}
            var Q62;
            {var subQ5=sQuery(id+"F0.wireOp",EDGE,"E14.top");Q62=makeQuery(id+"F0.imprint","IMPRINT",FACE,{"disambiguationData":[TD([[makeQuery(id+"F0.imprint","IMPRINT",EDGE,{"derivedFrom":subQ5}),-1.0]])]});}
            var Q63;
            {var subQ5=sQuery(id+"F0.wireOp",EDGE,"E15.top");Q63=makeQuery(id+"F0.imprint","IMPRINT",FACE,{"disambiguationData":[TD([[makeQuery(id+"F0.imprint","IMPRINT",EDGE,{"derivedFrom":subQ5}),-1.0]])]});}
            var Q64;
            {var subQ5=sQuery(id+"F0.wireOp",EDGE,"E16.top");Q64=makeQuery(id+"F0.imprint","IMPRINT",FACE,{"disambiguationData":[TD([[makeQuery(id+"F0.imprint","IMPRINT",EDGE,{"derivedFrom":subQ5}),-1.0]])]});}
            var Q65;
            {var subQ5=sQuery(id+"F0.wireOp",EDGE,"E17.top");Q65=makeQuery(id+"F0.imprint","IMPRINT",FACE,{"disambiguationData":[TD([[makeQuery(id+"F0.imprint","IMPRINT",EDGE,{"derivedFrom":subQ5}),-1.0]])]});}
            var Q66;
            {var subQ5=sQuery(id+"F0.wireOp",EDGE,"E18.top");Q66=makeQuery(id+"F0.imprint","IMPRINT",FACE,{"disambiguationData":[TD([[makeQuery(id+"F0.imprint","IMPRINT",EDGE,{"derivedFrom":subQ5}),-1.0]])]});}
            var Q67;
            {var subQ5=sQuery(id+"F0.wireOp",EDGE,"E19.top");Q67=makeQuery(id+"F0.imprint","IMPRINT",FACE,{"disambiguationData":[TD([[makeQuery(id+"F0.imprint","IMPRINT",EDGE,{"derivedFrom":subQ5}),-1.0]])]});}
            var Q68;
            {var subQ5=sQuery(id+"F0.wireOp",EDGE,"E20.top");Q68=makeQuery(id+"F0.imprint","IMPRINT",FACE,{"disambiguationData":[TD([[makeQuery(id+"F0.imprint","IMPRINT",EDGE,{"derivedFrom":subQ5}),-1.0]])]});}
            var Q69;
            {var subQ0=sQuery(id+"F0.wireOp",EDGE,"E17.left");var subQ1=sQuery(id+"F0.wireOp",EDGE,"E11.top");var subQ2=makeQuery(id+"F0.imprint","INTERSECT",VERTEX,{"derivedFrom":[subQ1,subQ0]});Q69=makeQuery(id+"F0.imprint","IMPRINT",FACE,{"disambiguationData":[TD([[makeQuery(id+"F0.imprint","IMPRINT",EDGE,{"disambiguationData":[TD([[subQ2,-1.0]])],"derivedFrom":subQ1}),1.0]])]});}
            var Q70;
            {var subQ0=sQuery(id+"F0.wireOp",EDGE,"E17.right");var subQ1=sQuery(id+"F0.wireOp",EDGE,"E12.bottom");var subQ2=makeQuery(id+"F0.imprint","INTERSECT",VERTEX,{"derivedFrom":[subQ1,subQ0]});Q70=makeQuery(id+"F0.imprint","IMPRINT",FACE,{"disambiguationData":[TD([[makeQuery(id+"F0.imprint","IMPRINT",EDGE,{"disambiguationData":[TD([[subQ2,-1.0]])],"derivedFrom":subQ1}),1.0]])]});}
            var Q71;
            {var subQ0=sQuery(id+"F0.wireOp",EDGE,"E18.right");var subQ1=sQuery(id+"F0.wireOp",EDGE,"E12.bottom");var subQ2=makeQuery(id+"F0.imprint","INTERSECT",VERTEX,{"derivedFrom":[subQ1,subQ0]});Q71=makeQuery(id+"F0.imprint","IMPRINT",FACE,{"disambiguationData":[TD([[makeQuery(id+"F0.imprint","IMPRINT",EDGE,{"disambiguationData":[TD([[subQ2,-1.0]])],"derivedFrom":subQ1}),1.0]])]});}
            var Q72;
            {var subQ0=sQuery(id+"F0.wireOp",EDGE,"E17.left");var subQ1=sQuery(id+"F0.wireOp",EDGE,"E12.top");var subQ2=makeQuery(id+"F0.imprint","INTERSECT",VERTEX,{"derivedFrom":[subQ1,subQ0]});Q72=makeQuery(id+"F0.imprint","IMPRINT",FACE,{"disambiguationData":[TD([[makeQuery(id+"F0.imprint","IMPRINT",EDGE,{"disambiguationData":[TD([[subQ2,-1.0]])],"derivedFrom":subQ1}),1.0]])]});}
            var Q73;
            {var subQ0=sQuery(id+"F0.wireOp",EDGE,"E17.left");var subQ1=sQuery(id+"F0.wireOp",EDGE,"E12.bottom");var subQ2=makeQuery(id+"F0.imprint","INTERSECT",VERTEX,{"derivedFrom":[subQ1,subQ0]});Q73=makeQuery(id+"F0.imprint","IMPRINT",FACE,{"disambiguationData":[TD([[makeQuery(id+"F0.imprint","IMPRINT",EDGE,{"disambiguationData":[TD([[subQ2,-1.0]])],"derivedFrom":subQ1}),1.0]])]});}
            var Q74;
            {var subQ0=sQuery(id+"F0.wireOp",EDGE,"E14.left");var subQ1=sQuery(id+"F0.wireOp",EDGE,"E11.bottom");var subQ2=makeQuery(id+"F0.imprint","INTERSECT",VERTEX,{"derivedFrom":[subQ1,subQ0]});Q74=makeQuery(id+"F0.imprint","IMPRINT",FACE,{"disambiguationData":[TD([[makeQuery(id+"F0.imprint","IMPRINT",EDGE,{"disambiguationData":[TD([[subQ2,-1.0]])],"derivedFrom":subQ1}),-1.0]])]});}
            var Q75;
            {var subQ0=sQuery(id+"F0.wireOp",EDGE,"E32.trimOffspring");var subQ1=sQuery(id+"F0.wireOp",EDGE,"E11.bottom");var subQ2=makeQuery(id+"F0.imprint","INTERSECT",VERTEX,{"derivedFrom":[subQ1,subQ0]});Q75=makeQuery(id+"F0.imprint","IMPRINT",FACE,{"disambiguationData":[TD([[makeQuery(id+"F0.imprint","IMPRINT",EDGE,{"disambiguationData":[TD([[subQ2,1.0]])],"derivedFrom":subQ1}),1.0]])]});}
            var Q76;
            {var subQ0=sQuery(id+"F0.wireOp",EDGE,"E32.trimOffspring");var subQ1=sQuery(id+"F0.wireOp",EDGE,"E12.bottom");var subQ2=makeQuery(id+"F0.imprint","INTERSECT",VERTEX,{"derivedFrom":[subQ1,subQ0]});Q76=makeQuery(id+"F0.imprint","IMPRINT",FACE,{"disambiguationData":[TD([[makeQuery(id+"F0.imprint","IMPRINT",EDGE,{"disambiguationData":[TD([[subQ2,1.0]])],"derivedFrom":subQ1}),1.0]])]});}
            var Q77;
            {var subQ0=sQuery(id+"F0.wireOp",EDGE,"E32.trimOffspring");var subQ1=sQuery(id+"F0.wireOp",EDGE,"E13.bottom");var subQ2=makeQuery(id+"F0.imprint","INTERSECT",VERTEX,{"derivedFrom":[subQ1,subQ0]});Q77=makeQuery(id+"F0.imprint","IMPRINT",FACE,{"disambiguationData":[TD([[makeQuery(id+"F0.imprint","IMPRINT",EDGE,{"disambiguationData":[TD([[subQ2,1.0]])],"derivedFrom":subQ1}),1.0]])]});}
            var Q78;
            {var subQ0=sQuery(id+"F0.wireOp",EDGE,"E14.left");var subQ1=sQuery(id+"F0.wireOp",EDGE,"E13.top");var subQ2=makeQuery(id+"F0.imprint","INTERSECT",VERTEX,{"derivedFrom":[subQ1,subQ0]});Q78=makeQuery(id+"F0.imprint","IMPRINT",FACE,{"disambiguationData":[TD([[makeQuery(id+"F0.imprint","IMPRINT",EDGE,{"disambiguationData":[TD([[subQ2,-1.0]])],"derivedFrom":subQ1}),1.0]])]});}
            var Q79;
            {var subQ0=sQuery(id+"F0.wireOp",EDGE,"E15.left");var subQ1=sQuery(id+"F0.wireOp",EDGE,"E13.top");var subQ2=makeQuery(id+"F0.imprint","INTERSECT",VERTEX,{"derivedFrom":[subQ1,subQ0]});Q79=makeQuery(id+"F0.imprint","IMPRINT",FACE,{"disambiguationData":[TD([[makeQuery(id+"F0.imprint","IMPRINT",EDGE,{"disambiguationData":[TD([[subQ2,-1.0]])],"derivedFrom":subQ1}),1.0]])]});}
            var Q80;
            {var subQ0=sQuery(id+"F0.wireOp",EDGE,"E16.left");var subQ1=sQuery(id+"F0.wireOp",EDGE,"E13.top");var subQ2=makeQuery(id+"F0.imprint","INTERSECT",VERTEX,{"derivedFrom":[subQ1,subQ0]});Q80=makeQuery(id+"F0.imprint","IMPRINT",FACE,{"disambiguationData":[TD([[makeQuery(id+"F0.imprint","IMPRINT",EDGE,{"disambiguationData":[TD([[subQ2,-1.0]])],"derivedFrom":subQ1}),1.0]])]});}
            var Q81;
            {var subQ0=sQuery(id+"F0.wireOp",EDGE,"E18.left");var subQ1=sQuery(id+"F0.wireOp",EDGE,"E13.top");var subQ2=makeQuery(id+"F0.imprint","INTERSECT",VERTEX,{"derivedFrom":[subQ1,subQ0]});Q81=makeQuery(id+"F0.imprint","IMPRINT",FACE,{"disambiguationData":[TD([[makeQuery(id+"F0.imprint","IMPRINT",EDGE,{"disambiguationData":[TD([[subQ2,-1.0]])],"derivedFrom":subQ1}),1.0]])]});}
            var Q82;
            {var subQ0=sQuery(id+"F0.wireOp",EDGE,"E19.left");var subQ1=sQuery(id+"F0.wireOp",EDGE,"E13.top");var subQ2=makeQuery(id+"F0.imprint","INTERSECT",VERTEX,{"derivedFrom":[subQ1,subQ0]});Q82=makeQuery(id+"F0.imprint","IMPRINT",FACE,{"disambiguationData":[TD([[makeQuery(id+"F0.imprint","IMPRINT",EDGE,{"disambiguationData":[TD([[subQ2,-1.0]])],"derivedFrom":subQ1}),1.0]])]});}
            var Q83;
            {var subQ0=sQuery(id+"F0.wireOp",EDGE,"E20.left");var subQ1=sQuery(id+"F0.wireOp",EDGE,"E13.top");var subQ2=makeQuery(id+"F0.imprint","INTERSECT",VERTEX,{"derivedFrom":[subQ1,subQ0]});Q83=makeQuery(id+"F0.imprint","IMPRINT",FACE,{"disambiguationData":[TD([[makeQuery(id+"F0.imprint","IMPRINT",EDGE,{"disambiguationData":[TD([[subQ2,-1.0]])],"derivedFrom":subQ1}),1.0]])]});}
            var Q84;
            {var subQ0=sQuery(id+"F0.wireOp",EDGE,"E23.trimOffspring");var subQ1=sQuery(id+"F0.wireOp",EDGE,"E13.bottom");var subQ2=makeQuery(id+"F0.imprint","INTERSECT",VERTEX,{"derivedFrom":[subQ1,subQ0]});Q84=makeQuery(id+"F0.imprint","IMPRINT",FACE,{"disambiguationData":[TD([[makeQuery(id+"F0.imprint","IMPRINT",EDGE,{"disambiguationData":[TD([[subQ2,-1.0]])],"derivedFrom":subQ1}),1.0]])]});}
            var Q85;
            {var subQ0=sQuery(id+"F0.wireOp",EDGE,"E23.trimOffspring");var subQ1=sQuery(id+"F0.wireOp",EDGE,"E12.bottom");var subQ2=makeQuery(id+"F0.imprint","INTERSECT",VERTEX,{"derivedFrom":[subQ1,subQ0]});Q85=makeQuery(id+"F0.imprint","IMPRINT",FACE,{"disambiguationData":[TD([[makeQuery(id+"F0.imprint","IMPRINT",EDGE,{"disambiguationData":[TD([[subQ2,-1.0]])],"derivedFrom":subQ1}),1.0]])]});}
            var Q86;
            {var subQ0=sQuery(id+"F0.wireOp",EDGE,"E20.left");var subQ1=sQuery(id+"F0.wireOp",EDGE,"E11.bottom");var subQ2=makeQuery(id+"F0.imprint","INTERSECT",VERTEX,{"derivedFrom":[subQ1,subQ0]});Q86=makeQuery(id+"F0.imprint","IMPRINT",FACE,{"disambiguationData":[TD([[makeQuery(id+"F0.imprint","IMPRINT",EDGE,{"disambiguationData":[TD([[subQ2,-1.0]])],"derivedFrom":subQ1}),-1.0]])]});}
            var Q87;
            {var subQ0=sQuery(id+"F0.wireOp",EDGE,"E19.left");var subQ1=sQuery(id+"F0.wireOp",EDGE,"E11.bottom");var subQ2=makeQuery(id+"F0.imprint","INTERSECT",VERTEX,{"derivedFrom":[subQ1,subQ0]});Q87=makeQuery(id+"F0.imprint","IMPRINT",FACE,{"disambiguationData":[TD([[makeQuery(id+"F0.imprint","IMPRINT",EDGE,{"disambiguationData":[TD([[subQ2,-1.0]])],"derivedFrom":subQ1}),-1.0]])]});}
            var Q88;
            {var subQ0=sQuery(id+"F0.wireOp",EDGE,"E18.left");var subQ1=sQuery(id+"F0.wireOp",EDGE,"E11.bottom");var subQ2=makeQuery(id+"F0.imprint","INTERSECT",VERTEX,{"derivedFrom":[subQ1,subQ0]});Q88=makeQuery(id+"F0.imprint","IMPRINT",FACE,{"disambiguationData":[TD([[makeQuery(id+"F0.imprint","IMPRINT",EDGE,{"disambiguationData":[TD([[subQ2,-1.0]])],"derivedFrom":subQ1}),-1.0]])]});}
            var Q89;
            {var subQ0=sQuery(id+"F0.wireOp",EDGE,"E17.left");var subQ1=sQuery(id+"F0.wireOp",EDGE,"E11.bottom");var subQ2=makeQuery(id+"F0.imprint","INTERSECT",VERTEX,{"derivedFrom":[subQ1,subQ0]});Q89=makeQuery(id+"F0.imprint","IMPRINT",FACE,{"disambiguationData":[TD([[makeQuery(id+"F0.imprint","IMPRINT",EDGE,{"disambiguationData":[TD([[subQ2,-1.0]])],"derivedFrom":subQ1}),-1.0]])]});}
            var Q90;
            {var subQ0=sQuery(id+"F0.wireOp",EDGE,"E16.left");var subQ1=sQuery(id+"F0.wireOp",EDGE,"E11.bottom");var subQ2=makeQuery(id+"F0.imprint","INTERSECT",VERTEX,{"derivedFrom":[subQ1,subQ0]});Q90=makeQuery(id+"F0.imprint","IMPRINT",FACE,{"disambiguationData":[TD([[makeQuery(id+"F0.imprint","IMPRINT",EDGE,{"disambiguationData":[TD([[subQ2,-1.0]])],"derivedFrom":subQ1}),-1.0]])]});}
            var Q91;
            {var subQ0=sQuery(id+"F0.wireOp",EDGE,"E15.left");var subQ1=sQuery(id+"F0.wireOp",EDGE,"E11.bottom");var subQ2=makeQuery(id+"F0.imprint","INTERSECT",VERTEX,{"derivedFrom":[subQ1,subQ0]});Q91=makeQuery(id+"F0.imprint","IMPRINT",FACE,{"disambiguationData":[TD([[makeQuery(id+"F0.imprint","IMPRINT",EDGE,{"disambiguationData":[TD([[subQ2,-1.0]])],"derivedFrom":subQ1}),-1.0]])]});}
            var Q92;
            {var subQ0=sQuery(id+"F0.wireOp",EDGE,"E17.left");var subQ1=sQuery(id+"F0.wireOp",EDGE,"E13.top");var subQ2=makeQuery(id+"F0.imprint","INTERSECT",VERTEX,{"derivedFrom":[subQ1,subQ0]});Q92=makeQuery(id+"F0.imprint","IMPRINT",FACE,{"disambiguationData":[TD([[makeQuery(id+"F0.imprint","IMPRINT",EDGE,{"disambiguationData":[TD([[subQ2,-1.0]])],"derivedFrom":subQ1}),1.0]])]});}
            var Q93;
            {var subQ0=sQuery(id+"F0.wireOp",EDGE,"E23.trimOffspring");var subQ1=sQuery(id+"F0.wireOp",EDGE,"E11.bottom");var subQ2=makeQuery(id+"F0.imprint","INTERSECT",VERTEX,{"derivedFrom":[subQ1,subQ0]});Q93=makeQuery(id+"F0.imprint","IMPRINT",FACE,{"disambiguationData":[TD([[makeQuery(id+"F0.imprint","IMPRINT",EDGE,{"disambiguationData":[TD([[subQ2,-1.0]])],"derivedFrom":subQ1}),1.0]])]});}
            extrude(context, id + "F1", {"entities" : qUnion([Q0, Q1, Q2, Q3, Q4, Q5, Q6, Q7, Q8, Q9, Q10, Q11, Q12, Q13, Q14, Q15, Q16, Q17, Q18, Q19, Q20, Q21, Q22, Q23, Q24, Q25, Q26, Q27, Q28, Q29, Q30, Q31, Q32, Q33, Q34, Q35, Q36, Q37, Q38, Q39, Q40, Q41, Q42, Q43, Q44, Q45, Q46, Q47, Q48, Q49, Q50, Q51, Q52, Q53, Q54, Q55, Q56, Q57, Q58, Q59, Q60, Q61, Q62, Q63, Q64, Q65, Q66, Q67, Q68, Q69, Q70, Q71, Q72, Q73, Q74, Q75, Q76, Q77, Q78, Q79, Q80, Q81, Q82, Q83, Q84, Q85, Q86, Q87, Q88, Q89, Q90, Q91, Q92, Q93]), "depth" : 6.35 * mm, "offsetDistance" : 25.4 * mm, "hasDraft" : true, "draftAngle" : 2 * degree, "draftPullDirection" : true});
        }
        {
            var Q0;
            Q0=makeQuery(id+"F1.opExtrude","CAP_FACE",FACE,{"disambiguationData":[OSD([sQuery(id+"F0.wireOp",EDGE,"E0.bottom"),sQuery(id+"F0.wireOp",EDGE,"E0.top"),sQuery(id+"F0.wireOp",EDGE,"E0.left"),sQuery(id+"F0.wireOp",EDGE,"E0.right"),sQuery(id+"F0.wireOp",EDGE,"4c8447cf-2a79-4bae-a500-c6cda96fcce5.0"),sQuery(id+"F0.wireOp",EDGE,"4c8447cf-2a79-4bae-a500-c6cda96fcce5.1"),sQuery(id+"F0.wireOp",EDGE,"4c8447cf-2a79-4bae-a500-c6cda96fcce5.2"),sQuery(id+"F0.wireOp",EDGE,"4c8447cf-2a79-4bae-a500-c6cda96fcce5.3"),sQuery(id+"F0.wireOp",EDGE,"E11.bottom"),sQuery(id+"F0.wireOp",EDGE,"E11.top"),sQuery(id+"F0.wireOp",EDGE,"E12.bottom"),sQuery(id+"F0.wireOp",EDGE,"E12.top"),sQuery(id+"F0.wireOp",EDGE,"E13.bottom"),sQuery(id+"F0.wireOp",EDGE,"E13.top"),sQuery(id+"F0.wireOp",EDGE,"E14.left"),sQuery(id+"F0.wireOp",EDGE,"E14.right"),sQuery(id+"F0.wireOp",EDGE,"E15.left"),sQuery(id+"F0.wireOp",EDGE,"E15.right"),sQuery(id+"F0.wireOp",EDGE,"E16.left"),sQuery(id+"F0.wireOp",EDGE,"E16.right"),sQuery(id+"F0.wireOp",EDGE,"E17.left"),sQuery(id+"F0.wireOp",EDGE,"E17.right"),sQuery(id+"F0.wireOp",EDGE,"E18.left"),sQuery(id+"F0.wireOp",EDGE,"E18.right"),sQuery(id+"F0.wireOp",EDGE,"E19.left"),sQuery(id+"F0.wireOp",EDGE,"E19.right"),sQuery(id+"F0.wireOp",EDGE,"E20.left"),sQuery(id+"F0.wireOp",EDGE,"E20.right")])],"isStart":true});
            extrude(context, id + "F2", {"entities" : qUnion([Q0]), "operationType" : NewBodyOperationType.ADD, "depth" : 6.35 * mm, "offsetDistance" : 25.4 * mm, "hasDraft" : true, "draftAngle" : 2 * degree});
        }
        {
            var Q0;
            Q0=makeQuery(id+"F1.opExtrude","CAP_FACE",FACE,{"disambiguationData":[OSD([sQuery(id+"F0.wireOp",EDGE,"E0.bottom"),sQuery(id+"F0.wireOp",EDGE,"E0.top"),sQuery(id+"F0.wireOp",EDGE,"E0.left"),sQuery(id+"F0.wireOp",EDGE,"E0.right"),sQuery(id+"F0.wireOp",EDGE,"4c8447cf-2a79-4bae-a500-c6cda96fcce5.0"),sQuery(id+"F0.wireOp",EDGE,"4c8447cf-2a79-4bae-a500-c6cda96fcce5.1"),sQuery(id+"F0.wireOp",EDGE,"4c8447cf-2a79-4bae-a500-c6cda96fcce5.2"),sQuery(id+"F0.wireOp",EDGE,"4c8447cf-2a79-4bae-a500-c6cda96fcce5.3"),sQuery(id+"F0.wireOp",EDGE,"E11.bottom"),sQuery(id+"F0.wireOp",EDGE,"E11.top"),sQuery(id+"F0.wireOp",EDGE,"E12.bottom"),sQuery(id+"F0.wireOp",EDGE,"E12.top"),sQuery(id+"F0.wireOp",EDGE,"E13.bottom"),sQuery(id+"F0.wireOp",EDGE,"E13.top"),sQuery(id+"F0.wireOp",EDGE,"E14.left"),sQuery(id+"F0.wireOp",EDGE,"E14.right"),sQuery(id+"F0.wireOp",EDGE,"E15.left"),sQuery(id+"F0.wireOp",EDGE,"E15.right"),sQuery(id+"F0.wireOp",EDGE,"E16.left"),sQuery(id+"F0.wireOp",EDGE,"E16.right"),sQuery(id+"F0.wireOp",EDGE,"E17.left"),sQuery(id+"F0.wireOp",EDGE,"E17.right"),sQuery(id+"F0.wireOp",EDGE,"E18.left"),sQuery(id+"F0.wireOp",EDGE,"E18.right"),sQuery(id+"F0.wireOp",EDGE,"E19.left"),sQuery(id+"F0.wireOp",EDGE,"E19.right"),sQuery(id+"F0.wireOp",EDGE,"E20.left"),sQuery(id+"F0.wireOp",EDGE,"E20.right")])],"isStart":false});
            var Q1;
            Q1=makeQuery(id+"F2.opExtrude","CAP_FACE",FACE,{"disambiguationData":[OSD([sQuery(id+"F0.wireOp",EDGE,"E0.bottom"),sQuery(id+"F0.wireOp",EDGE,"E0.top"),sQuery(id+"F0.wireOp",EDGE,"E0.left"),sQuery(id+"F0.wireOp",EDGE,"E0.right"),sQuery(id+"F0.wireOp",EDGE,"4c8447cf-2a79-4bae-a500-c6cda96fcce5.0"),sQuery(id+"F0.wireOp",EDGE,"4c8447cf-2a79-4bae-a500-c6cda96fcce5.1"),sQuery(id+"F0.wireOp",EDGE,"4c8447cf-2a79-4bae-a500-c6cda96fcce5.2"),sQuery(id+"F0.wireOp",EDGE,"4c8447cf-2a79-4bae-a500-c6cda96fcce5.3"),sQuery(id+"F0.wireOp",EDGE,"E11.bottom"),sQuery(id+"F0.wireOp",EDGE,"E11.top"),sQuery(id+"F0.wireOp",EDGE,"E12.bottom"),sQuery(id+"F0.wireOp",EDGE,"E12.top"),sQuery(id+"F0.wireOp",EDGE,"E13.bottom"),sQuery(id+"F0.wireOp",EDGE,"E13.top"),sQuery(id+"F0.wireOp",EDGE,"E14.left"),sQuery(id+"F0.wireOp",EDGE,"E14.right"),sQuery(id+"F0.wireOp",EDGE,"E15.left"),sQuery(id+"F0.wireOp",EDGE,"E15.right"),sQuery(id+"F0.wireOp",EDGE,"E16.left"),sQuery(id+"F0.wireOp",EDGE,"E16.right"),sQuery(id+"F0.wireOp",EDGE,"E17.left"),sQuery(id+"F0.wireOp",EDGE,"E17.right"),sQuery(id+"F0.wireOp",EDGE,"E18.left"),sQuery(id+"F0.wireOp",EDGE,"E18.right"),sQuery(id+"F0.wireOp",EDGE,"E19.left"),sQuery(id+"F0.wireOp",EDGE,"E19.right"),sQuery(id+"F0.wireOp",EDGE,"E20.left"),sQuery(id+"F0.wireOp",EDGE,"E20.right")])],"isStart":false});
            fillet(context, id + "F3", {"entities" : qUnion([Q0, Q1]), "radius" : 0.28 * mm, "tangentPropagation" : true, "allowEdgeOverflow" : false});
        }
    });
